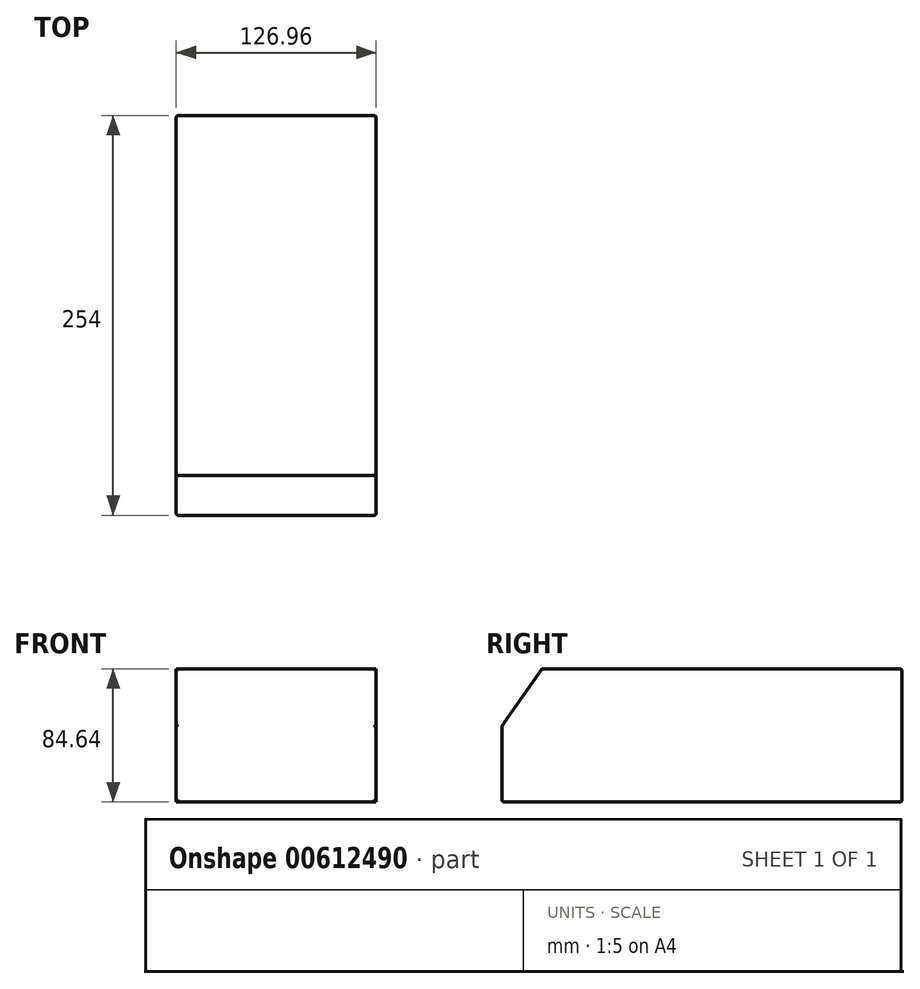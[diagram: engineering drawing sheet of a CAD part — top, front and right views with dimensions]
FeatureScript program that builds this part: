
annotation { "Feature Type Name" : "Feature", "Feature Type Description" : "" }
export const myFeature = defineFeature(function(context is Context, id is Id, definition is map)
    precondition{}
    {
        {
            var Q0;
            Q0=qCreatedBy(makeId("Front.planeOp"),FACE);
            var sketch = newSketch(context, id + "F0", { "sketchPlane" : qUnion([Q0])});
            skLineSegment(sketch, "E0.bottom", {"start": v(-62.65, 44.47) * mm, "end": v(64.3, 44.47) * mm});
            skLineSegment(sketch, "E0.top", {"start": v(-62.65, -40.17) * mm, "end": v(64.3, -40.17) * mm});
            skLineSegment(sketch, "E0.left", {"start": v(-62.65, 44.47) * mm, "end": v(-62.65, -40.17) * mm});
            skLineSegment(sketch, "E0.right", {"start": v(64.3, 44.47) * mm, "end": v(64.3, -40.17) * mm});
            skSolve(sketch);
        }
        {
            var Q0;
            Q0 = qSketchRegion(id + "F0", true);
            extrude(context, id + "F1", {"entities" : qUnion([Q0]), "endBound" : BoundingType.SYMMETRIC, "depth" : 254 * mm, "offsetDistance" : 25.4 * mm});
        }
        {
            var Q0;
            Q0=makeQuery(id+"F1.opExtrude","CAP_EDGE",EDGE,{"disambiguationData":[OSD([sQuery(id+"F0.wireOp",EDGE,"E0.bottom")])],"isStart":false});
            chamfer(context, id + "F2", {"entities" : qUnion([Q0]), "chamferType" : ChamferType.OFFSET_ANGLE, "width" : 25.4 * mm, "oppositeDirection" : false, "angle" : 55 * degree, "tangentPropagation" : true});
        }
        {
            var Q0;
            Q0=makeQuery(id+"F1.opExtrude","CAP_FACE",FACE,{"disambiguationData":[OSD([sQuery(id+"F0.wireOp",EDGE,"E0.bottom"),sQuery(id+"F0.wireOp",EDGE,"E0.top"),sQuery(id+"F0.wireOp",EDGE,"E0.left"),sQuery(id+"F0.wireOp",EDGE,"E0.right")])],"isStart":true});
            var Q1;
            Q1=makeQuery(id+"F1.opExtrude","CAP_FACE",FACE,{"disambiguationData":[OSD([sQuery(id+"F0.wireOp",EDGE,"E0.bottom"),sQuery(id+"F0.wireOp",EDGE,"E0.top"),sQuery(id+"F0.wireOp",EDGE,"E0.left"),sQuery(id+"F0.wireOp",EDGE,"E0.right")])],"isStart":false});
            fillet(context, id + "F3", {"entities" : qUnion([Q0, Q1]), "radius" : 1.27 * mm, "tangentPropagation" : true, "allowEdgeOverflow" : false});
        }
    });
